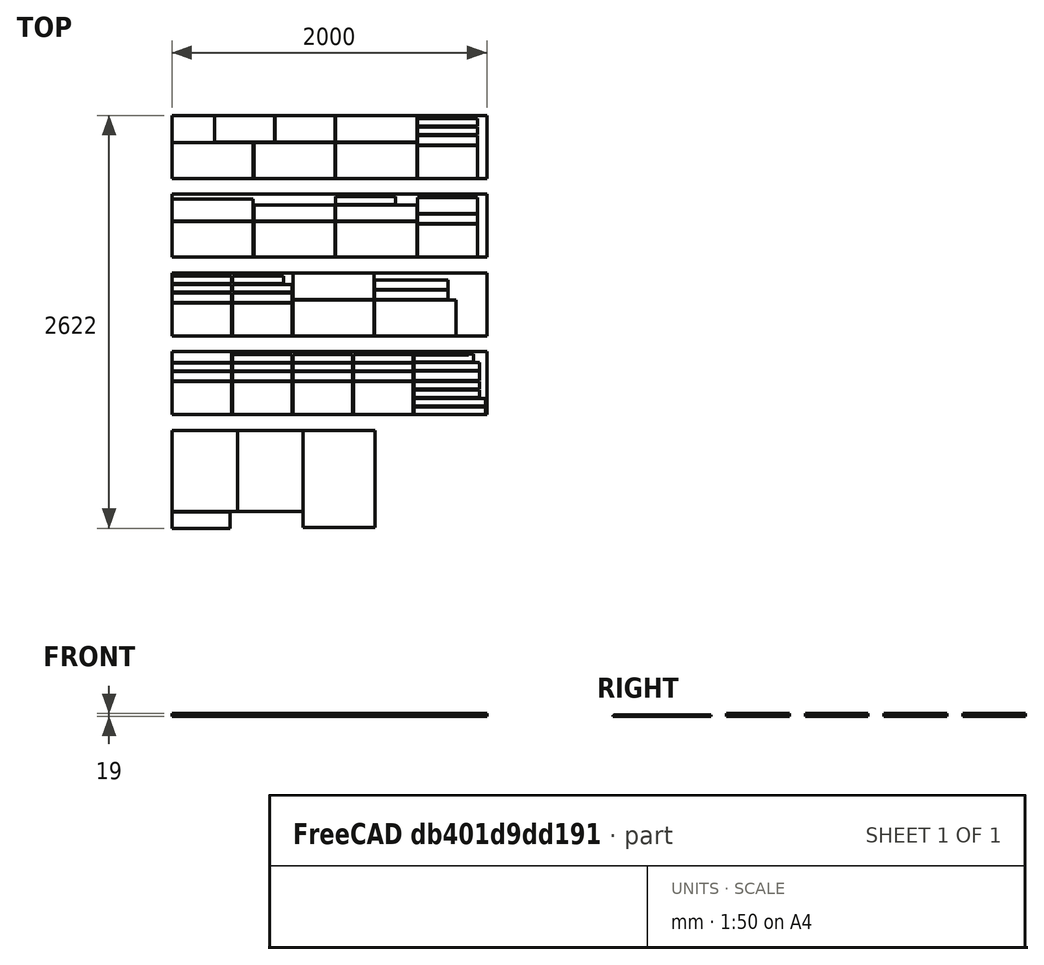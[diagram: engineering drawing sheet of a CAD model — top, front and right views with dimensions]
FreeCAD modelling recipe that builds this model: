
FCSTD DOCUMENT  (FreeCAD 0.16R)
Label: Schnittpäne
License: All rights reserved
LicenseURL: http://en.wikipedia.org/wiki/All_rights_reserved
objects: Part::Box×65, App::DocumentObjectGroup×23
note: 65 computed .brp shape members not serialized (recipe doc carries the construction recipe); baked Part::Feature solids carry a one-line shape summary decoded from their .brp

FEATURE [Part::Box] Box  label="BRETT"
  Height = 18
  Length = 2000
  Placement = pos=(0,0,-1) rot=(0,0,1;0rad)
  Width = 400
FEATURE [Part::Box] Box001  label="Dach Front Big"
  Height = 18
  Length = 380
  Placement = pos=(0,332,0) rot=(0,0,1;0rad)
  Width = 69
FEATURE [Part::Box] Box002  label="Dach Back small"
  Height = 18
  Length = 380
  Placement = pos=(384,332,0) rot=(0,0,1;0rad)
  Width = 50
FEATURE [Part::Box] Box003  label="Zarge Back outer upper"
  Height = 18
  Length = 380
  Placement = pos=(1152,214,0) rot=(0,0,1;0rad)
  Width = 60
FEATURE [Part::Box] Box004  label="Zarge Back outer lower "
  Height = 18
  Length = 380
  Placement = pos=(1152,278,0) rot=(0,0,1;0rad)
  Width = 50
FEATURE [Part::Box] Box005  label="Zarge Front inner"
  Height = 18
  Length = 380
  Placement = pos=(1152,0,0) rot=(0,0,1;0rad)
  Width = 210
FEATURE [Part::Box] Box007  label="Zarge Front outer lower"
  Height = 18
  Length = 380
  Placement = pos=(768,278,0) rot=(0,0,1;0rad)
  Width = 50
FEATURE [Part::Box] Box008  label="Zarge Back inner"
  Height = 18
  Length = 380
  Placement = pos=(768,0,0) rot=(0,0,1;0rad)
  Width = 210
FEATURE [Part::Box] Box006  label="Zarge Front outer upper"
  Height = 18
  Length = 380
  Placement = pos=(768,214,0) rot=(0,0,1;0rad)
  Width = 60
FEATURE [Part::Box] Box009  label="Boden Back with Hole"
  Height = 18
  Length = 380
  Placement = pos=(1560,1278,0) rot=(0,0,1;0rad)
  Width = 100
FEATURE [Part::Box] Box010  label="Boden Flogloch outer upper"
  Height = 18
  Length = 380
  Placement = pos=(1152,332,0) rot=(0,0,1;0rad)
  Width = 50
FEATURE [Part::Box] Box014  label="Zarge Front outer lower001"
  Height = 18
  Length = 380
  Placement = pos=(0,278,0) rot=(0,0,1;0rad)
  Width = 50
FEATURE [Part::Box] Box015  label="Zarge Back inner001"
  Height = 18
  Length = 380
  Placement = pos=(384,0,0) rot=(0,0,1;0rad)
  Width = 210
FEATURE [Part::Box] Box016  label="Zarge Front outer upper001"
  Height = 18
  Length = 380
  Placement = pos=(0,214,0) rot=(0,0,1;0rad)
  Width = 60
FEATURE [Part::Box] Box012  label="Zarge Back outer lower 001"
  Height = 18
  Length = 380
  Placement = pos=(384,278,0) rot=(0,0,1;0rad)
  Width = 50
FEATURE [Part::Box] Box013  label="Zarge Front inner001"
  Height = 18
  Length = 380
  Width = 210
FEATURE [Part::Box] Box017  label="Boden Fluglochverschluss"
  Height = 18
  Length = 380
  Placement = pos=(1536,334,0) rot=(0,0,1;0rad)
  Width = 50
FEATURE [Part::Box] Box011  label="Zarge Back outer upper001"
  Height = 18
  Length = 380
  Placement = pos=(384,214,0) rot=(0,0,1;0rad)
  Width = 60
FEATURE [Part::Box] Box021  label="Boden Seite rechts unten"
  Height = 18
  Length = 466
  Placement = pos=(1288,731,0) rot=(0,0,1;0rad)
  Width = 60
FEATURE [App::DocumentObjectGroup] Gruppe014  label="Gruppe 380 Zarge"
  Group = -> [Box003,Box004,Box005,Box007,Box008,Box006]
FEATURE [App::DocumentObjectGroup] Gruppe016  label="Gruppe 380 Zarge2"
  Group = -> [Box012,Box013,Box014,Box015,Box016,Box011]
FEATURE [Part::Box] Box022  label="BRETT2"
  Height = 18
  Length = 2000
  Placement = pos=(0,500,-1) rot=(0,0,1;0rad)
  Width = 400
FEATURE [Part::Box] Box023  label="Boden Seite links unten"
  Height = 18
  Length = 466
  Placement = pos=(1288,795,0) rot=(0,0,1;0rad)
  Width = 60
FEATURE [App::DocumentObjectGroup] Gruppe009  label="Gruppe 466"
  Group = -> [Box021,Box023]
FEATURE [Part::Box] Box024  label="Boden Seite rechts oben"
  Height = 18
  Length = 456
  Placement = pos=(1536,0,0) rot=(0,0,1;0rad)
  Width = 50
FEATURE [Part::Box] Box025  label="Boden Seite links oben"
  Height = 18
  Length = 456
  Placement = pos=(1536,54,0) rot=(0,0,1;0rad)
  Width = 50
FEATURE [App::DocumentObjectGroup] Gruppe008  label="Gruppe 456"
  Group = -> [Box024,Box025]
FEATURE [Part::Box] Box026  label="Boden fuß vorne"
  Height = 18
  Length = 416
  Placement = pos=(1536,108,0) rot=(0,0,1;0rad)
  Width = 50
FEATURE [Part::Box] Box027  label="Boden fuß hinten unten"
  Height = 18
  Length = 416
  Placement = pos=(1536,280,0) rot=(0,0,1;0rad)
  Width = 50
FEATURE [Part::Box] Box028  label="Boden fuß hinten oben"
  Height = 18
  Length = 416
  Placement = pos=(1536,162,0) rot=(0,0,1;0rad)
  Width = 50
FEATURE [Part::Box] Box029  label="Boden Anflugbrett"
  Height = 18
  Length = 416
  Placement = pos=(1536,216,0) rot=(0,0,1;0rad)
  Width = 60
FEATURE [App::DocumentObjectGroup] Gruppe006  label="Gruppe 416"
  Group = -> [Box026,Box027,Box028,Box029]
FEATURE [Part::Box] Box030  label="Boden Varroalade Griff"
  Height = 18
  Length = 346
  Placement = pos=(1536,378,0) rot=(0,0,1;0rad)
  Width = 18
FEATURE [App::DocumentObjectGroup] Gruppe007  label="Gruppe 346"
  Group = -> [Box030]
FEATURE [Part::Box] Box035  label="Zarge Front inner002"
  Height = 18
  Length = 380
  Placement = pos=(0,500,0) rot=(0,0,1;0rad)
  Width = 210
FEATURE [Part::Box] Box032  label="Zarge Back inner002"
  Height = 18
  Length = 380
  Placement = pos=(384,500,0) rot=(0,0,1;0rad)
  Width = 210
FEATURE [Part::Box] Box031  label="Zarge Front outer lower002"
  Height = 18
  Length = 380
  Placement = pos=(0,778,0) rot=(0,0,1;0rad)
  Width = 50
FEATURE [Part::Box] Box034  label="Zarge Back outer lower 002"
  Height = 18
  Length = 380
  Placement = pos=(384,778,0) rot=(0,0,1;0rad)
  Width = 50
FEATURE [Part::Box] Box033  label="Zarge Front outer upper002"
  Height = 18
  Length = 380
  Placement = pos=(0,714,0) rot=(0,0,1;0rad)
  Width = 60
FEATURE [Part::Box] Box036  label="Zarge Back outer upper002"
  Height = 18
  Length = 380
  Placement = pos=(384,714,0) rot=(0,0,1;0rad)
  Width = 60
FEATURE [App::DocumentObjectGroup] Gruppe020  label="Gruppe 380 Zarge003"
  Group = -> [Box034,Box035,Box031,Box032,Box033,Box036]
FEATURE [Part::Box] Box037  label="Zarge Front inner003"
  Height = 18
  Length = 380
  Placement = pos=(1560,1500,0) rot=(0,0,1;0rad)
  Width = 210
FEATURE [Part::Box] Box038  label="Zarge Back inner003"
  Height = 18
  Length = 380
  Placement = pos=(1560,1000,0) rot=(0,0,1;0rad)
  Width = 210
FEATURE [Part::Box] Box039  label="Zarge Front outer lower003"
  Height = 18
  Length = 380
  Placement = pos=(1560,1778,0) rot=(0,0,1;0rad)
  Width = 50
FEATURE [Part::Box] Box040  label="Zarge Back outer lower 003"
  Height = 18
  Length = 380
  Placement = pos=(768,332,0) rot=(0,0,1;0rad)
  Width = 50
FEATURE [Part::Box] Box041  label="Zarge Front outer upper003"
  Height = 18
  Length = 380
  Placement = pos=(1560,1714,0) rot=(0,0,1;0rad)
  Width = 60
FEATURE [Part::Box] Box042  label="Zarge Back outer upper003"
  Height = 18
  Length = 380
  Placement = pos=(1560,1214,0) rot=(0,0,1;0rad)
  Width = 60
FEATURE [App::DocumentObjectGroup] Gruppe023  label="Gruppe 380 Zarge004"
  Group = -> [Box040,Box037,Box039,Box038,Box041,Box042]
FEATURE [Part::Box] Box043  label="BRETT 3"
  Height = 18
  Length = 2000
  Placement = pos=(0,1000,-1) rot=(0,0,1;0rad)
  Width = 400
FEATURE [Part::Box] Box044  label="Zarge 1 Links"
  Height = 18
  Length = 516
  Placement = pos=(0,1000,0) rot=(0,0,1;0rad)
  Width = 227
FEATURE [Part::Box] Box045  label="Zarge 1 Rechts"
  Height = 18
  Length = 516
  Placement = pos=(520,1000,0) rot=(0,0,1;0rad)
  Width = 227
FEATURE [App::DocumentObjectGroup] Gruppe012  label="Gruppe 516 Zarge "
  Group = -> [Box044,Box045]
FEATURE [App::DocumentObjectGroup] Gruppe002  label="Zarge1"
  Group = -> [Gruppe012,Gruppe014]
FEATURE [Part::Box] Box046  label="Zarge 1 Links001"
  Height = 18
  Length = 516
  Placement = pos=(0,1500,0) rot=(0,0,1;0rad)
  Width = 227
FEATURE [Part::Box] Box047  label="Zarge 1 Rechts001"
  Height = 18
  Length = 516
  Placement = pos=(1040,1000,0) rot=(0,0,1;0rad)
  Width = 227
FEATURE [App::DocumentObjectGroup] Gruppe013  label="Gruppe 516 Zarge 2"
  Group = -> [Box047,Box046]
FEATURE [App::DocumentObjectGroup] Gruppe004  label="Zarge2"
  Group = -> [Gruppe013,Gruppe016]
FEATURE [Part::Box] Box048  label="BRETT 4"
  Height = 18
  Length = 2000
  Placement = pos=(0,1500,-1) rot=(0,0,1;0rad)
  Width = 400
FEATURE [App::DocumentObjectGroup] Gruppe  label="Bretter"
  Group = -> [Box,Box022,Box043,Box048]
FEATURE [Part::Box] Box049  label="Zarge 1 Rechts002"
  Height = 18
  Length = 516
  Placement = pos=(1040,1500,0) rot=(0,0,1;0rad)
  Width = 227
FEATURE [Part::Box] Box050  label="Zarge 1 Links002"
  Height = 18
  Length = 516
  Placement = pos=(520,1500,0) rot=(0,0,1;0rad)
  Width = 227
FEATURE [App::DocumentObjectGroup] Gruppe019  label="Gruppe 516 Zarge 003"
  Group = -> [Box049,Box050]
FEATURE [App::DocumentObjectGroup] Gruppe018  label="Zarge3"
  Group = -> [Gruppe019,Gruppe020]
FEATURE [Part::Box] Box051  label="Boden Flogloch inner lower"
  Height = 18
  Length = 380
  Placement = pos=(0,832,0) rot=(0,0,1;0rad)
  Width = 50
FEATURE [Part::Box] Box052  label="Dach Seitenteile"
  Height = 18
  Length = 516
  Placement = pos=(0,1231,0) rot=(0,0,1;0rad)
  Width = 140
FEATURE [Part::Box] Box053  label="Boden Seite links"
  Height = 18
  Length = 516
  Placement = pos=(520,1231,0) rot=(0,0,1;0rad)
  Width = 100
FEATURE [Part::Box] Box054  label="Boden Seite rechts"
  Height = 18
  Length = 516
  Placement = pos=(1040,1231,0) rot=(0,0,1;0rad)
  Width = 100
FEATURE [App::DocumentObjectGroup] Gruppe010  label="Gruppe 516"
  Group = -> [Box053,Box054]
FEATURE [Part::Box] Box055  label="Boden unter Anflugbrett"
  Height = 18
  Length = 326
  Placement = pos=(384,832,0) rot=(0,0,1;0rad)
  Width = 50
FEATURE [App::DocumentObjectGroup] Gruppe011  label="Gruppe 326"
  Group = -> [Box055]
FEATURE [Part::Box] Box056  label="Zarge 1 Rechts003"
  Height = 18
  Length = 516
  Placement = pos=(768,500,0) rot=(0,0,1;0rad)
  Width = 227
FEATURE [Part::Box] Box060  label="Futterzarge Rechts"
  Height = 18
  Length = 516
  Placement = pos=(768,731,0) rot=(0,0,1;0rad)
  Width = 169
FEATURE [Part::Box] Box061  label="Futterzarge Links"
  Height = 18
  Length = 516
  Placement = pos=(1040,1731,0) rot=(0,0,1;0rad)
  Width = 169
FEATURE [Part::Box] Box062  label="Futterzarge Front"
  Height = 18
  Length = 380
  Placement = pos=(656,1731,0) rot=(0,0,1;0rad)
  Width = 169
FEATURE [Part::Box] Box063  label="Futterzarge hinten"
  Height = 18
  Length = 380
  Placement = pos=(272,1731,0) rot=(0,0,1;0rad)
  Width = 169
FEATURE [Part::Box] Box064  label=" Dach Unterseite Sperrholz"
  Height = 8
  Length = 416
  Placement = pos=(0,-616,0) rot=(0,0,1;0rad)
  Width = 516
FEATURE [Part::Box] Box065  label=" Dach Dach Material Wasserbeständig"
  Height = 8
  Length = 457
  Placement = pos=(834,-715,0) rot=(0,0,1;0rad)
  Width = 615
FEATURE [App::DocumentObjectGroup] Gruppe003  label="Dach"
  Group = -> [Box001,Box002,Box052,Box064,Box065]
FEATURE [Part::Box] Box066  label=" Futterzarge Unterseite Sperrholz"
  Height = 8
  Length = 416
  Placement = pos=(417,-616,0) rot=(0,0,1;0rad)
  Width = 516
FEATURE [App::DocumentObjectGroup] Gruppe026  label="Futterzarge"
  Group = -> [Box060,Box061,Box062,Box063,Box066]
FEATURE [Part::Box] Box067  label="Bearbeitungsloch Deckel"
  Height = 5
  Length = 370
  Placement = pos=(0,-722,0) rot=(0,0,1;0rad)
  Width = 105
FEATURE [Part::Box] Box068  label="Zarge 1 Rechts004"
  Height = 18
  Length = 516
  Placement = pos=(1288,500,0) rot=(0,0,1;0rad)
  Width = 227
FEATURE [App::DocumentObjectGroup] Gruppe022  label="Gruppe 516 Zarge 004"
  Group = -> [Box056,Box068]
FEATURE [App::DocumentObjectGroup] Gruppe021  label="Zarge4"
  Group = -> [Gruppe022,Gruppe023]
FEATURE [Part::Box] Box069  label="Boden Fluglochverschluss001"
  Height = 18
  Length = 380
  Placement = pos=(1040,1335,0) rot=(0,0,1;0rad)
  Width = 50
FEATURE [Part::Box] Box070  label="Boden Fluglochverschluss002"
  Height = 18
  Length = 380
  Placement = pos=(1560,1832,0) rot=(0,0,1;0rad)
  Width = 50
FEATURE [App::DocumentObjectGroup] Gruppe005  label="Gruppe 380"
  Group = -> [Box009,Box010,Box017,Box051,Box069,Box070]
FEATURE [App::DocumentObjectGroup] Gruppe001  label="Boden"
  Group = -> [Gruppe005,Gruppe006,Gruppe007,Gruppe008,Gruppe009,Gruppe010,Gruppe011,Box067]
